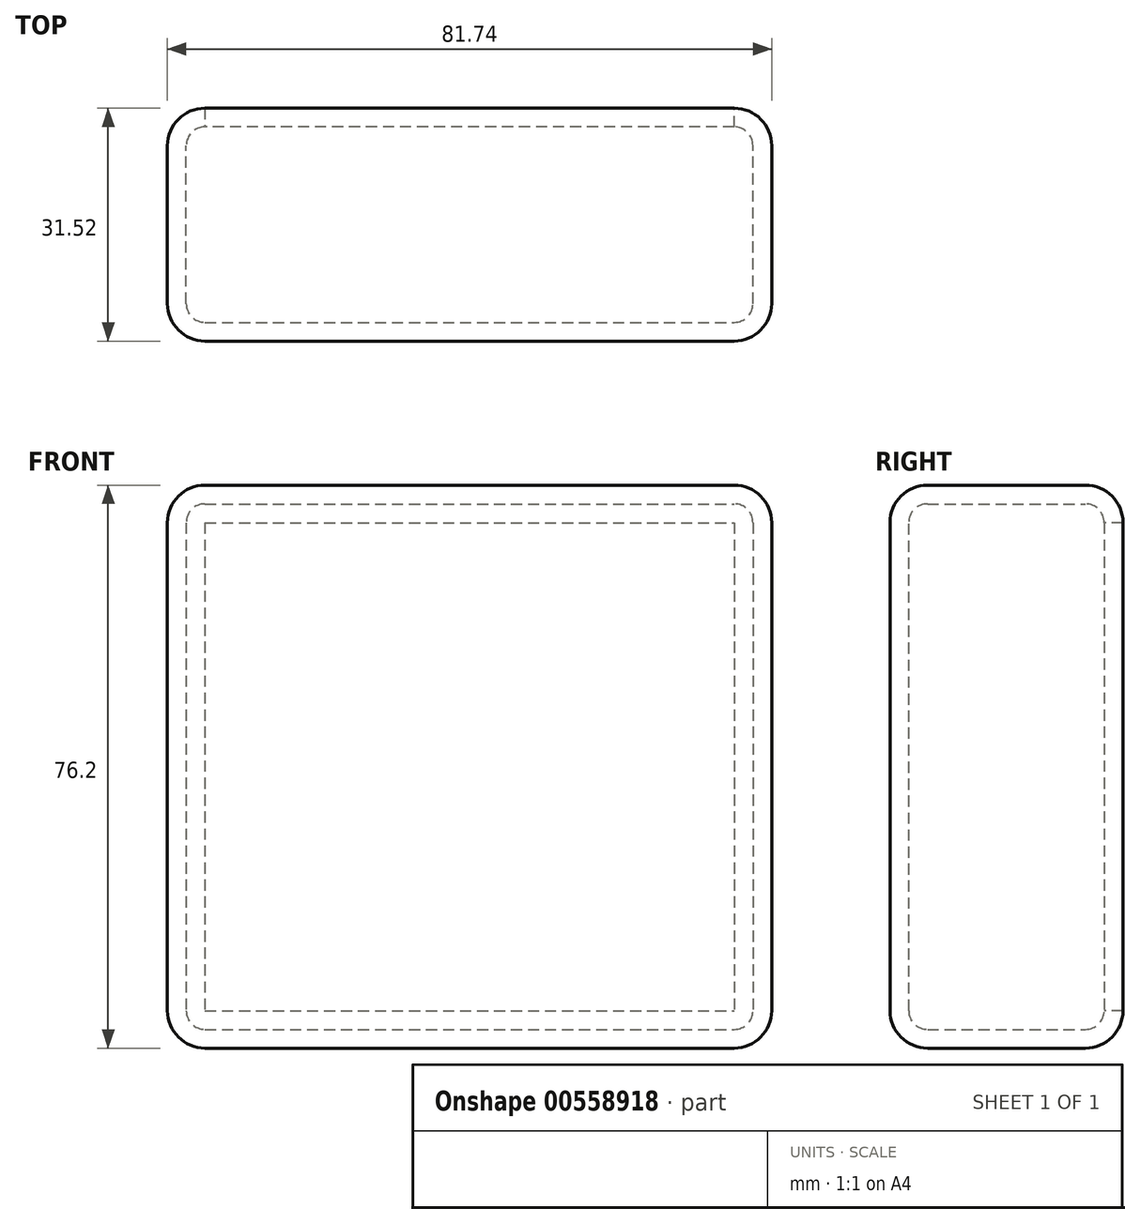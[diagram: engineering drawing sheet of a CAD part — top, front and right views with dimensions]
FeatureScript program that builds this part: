
annotation { "Feature Type Name" : "Feature", "Feature Type Description" : "" }
export const myFeature = defineFeature(function(context is Context, id is Id, definition is map)
    precondition{}
    {
        {
            var Q0;
            Q0=qCreatedBy(makeId("Top.planeOp"),FACE);
            var sketch = newSketch(context, id + "F0", { "sketchPlane" : qUnion([Q0])});
            skLineSegment(sketch, "E0.bottom", {"start": v(-40.87, 15.76) * mm, "end": v(40.87, 15.76) * mm});
            skLineSegment(sketch, "E0.top", {"start": v(-40.87, -15.76) * mm, "end": v(40.87, -15.76) * mm});
            skLineSegment(sketch, "E0.left", {"start": v(-40.87, 15.76) * mm, "end": v(-40.87, -15.76) * mm});
            skLineSegment(sketch, "E0.right", {"start": v(40.87, 15.76) * mm, "end": v(40.87, -15.76) * mm});
            skPoint(sketch, "E0.middle", {"position": v(0, 0) * mm});
            skSolve(sketch);
        }
        {
            var Q0;
            Q0=makeQuery(id+"F0.imprint","IMPRINT",FACE,{"disambiguationData":[TD([[makeQuery(id+"F0.imprint","IMPRINT",EDGE,{"derivedFrom":sQuery(id+"F0.wireOp",EDGE,"E0.bottom")}),-1.0]])]});
            extrude(context, id + "F1", {"entities" : qUnion([Q0]), "endBound" : BoundingType.SYMMETRIC, "depth" : 76.2 * mm, "offsetDistance" : 25.4 * mm});
        }
        {
            var Q0;
            Q0=makeQuery(id+"F1.opExtrude","SWEPT_EDGE",EDGE,{"disambiguationData":[OSD([sQuery(id+"F0.wireOp",EDGE,"E0.top"),sQuery(id+"F0.wireOp",EDGE,"E0.right")])]});
            var Q1;
            Q1=makeQuery(id+"F1.opExtrude","CAP_EDGE",EDGE,{"disambiguationData":[OSD([sQuery(id+"F0.wireOp",EDGE,"E0.top")])],"isStart":false});
            var Q2;
            Q2=makeQuery(id+"F1.opExtrude","SWEPT_EDGE",EDGE,{"disambiguationData":[OSD([sQuery(id+"F0.wireOp",EDGE,"E0.top"),sQuery(id+"F0.wireOp",EDGE,"E0.left")])]});
            var Q3;
            Q3=makeQuery(id+"F1.opExtrude","CAP_EDGE",EDGE,{"disambiguationData":[OSD([sQuery(id+"F0.wireOp",EDGE,"E0.top")])],"isStart":true});
            var Q4;
            Q4=makeQuery(id+"F1.opExtrude","SWEPT_EDGE",EDGE,{"disambiguationData":[OSD([sQuery(id+"F0.wireOp",EDGE,"E0.bottom"),sQuery(id+"F0.wireOp",EDGE,"E0.left")])]});
            var Q5;
            Q5=makeQuery(id+"F1.opExtrude","CAP_EDGE",EDGE,{"disambiguationData":[OSD([sQuery(id+"F0.wireOp",EDGE,"E0.left")])],"isStart":true});
            var Q6;
            Q6=makeQuery(id+"F1.opExtrude","CAP_EDGE",EDGE,{"disambiguationData":[OSD([sQuery(id+"F0.wireOp",EDGE,"E0.right")])],"isStart":true});
            var Q7;
            Q7=makeQuery(id+"F1.opExtrude","CAP_EDGE",EDGE,{"disambiguationData":[OSD([sQuery(id+"F0.wireOp",EDGE,"E0.bottom")])],"isStart":true});
            var Q8;
            Q8=makeQuery(id+"F1.opExtrude","CAP_EDGE",EDGE,{"disambiguationData":[OSD([sQuery(id+"F0.wireOp",EDGE,"E0.right")])],"isStart":false});
            var Q9;
            Q9=makeQuery(id+"F1.opExtrude","SWEPT_EDGE",EDGE,{"disambiguationData":[OSD([sQuery(id+"F0.wireOp",EDGE,"E0.bottom"),sQuery(id+"F0.wireOp",EDGE,"E0.right")])]});
            var Q10;
            Q10=makeQuery(id+"F1.opExtrude","CAP_EDGE",EDGE,{"disambiguationData":[OSD([sQuery(id+"F0.wireOp",EDGE,"E0.bottom")])],"isStart":false});
            var Q11;
            Q11=makeQuery(id+"F1.opExtrude","SWEPT_FACE",FACE,{"disambiguationData":[OSD([sQuery(id+"F0.wireOp",EDGE,"E0.left")])]});
            fillet(context, id + "F2", {"entities" : qUnion([Q0, Q1, Q2, Q3, Q4, Q5, Q6, Q7, Q8, Q9, Q10, Q11]), "radius" : 5.08 * mm, "tangentPropagation" : true, "allowEdgeOverflow" : false});
        }
        {
            var Q0;
            Q0=makeQuery(id+"F1.opExtrude","SWEPT_FACE",FACE,{"disambiguationData":[OSD([sQuery(id+"F0.wireOp",EDGE,"E0.bottom")])]});
            shell(context, id + "F3", {"entities" : qUnion([Q0]), "thickness" : 2.54 * mm});
        }
    });
